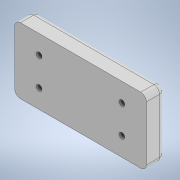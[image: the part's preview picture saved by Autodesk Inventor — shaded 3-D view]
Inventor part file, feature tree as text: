
AUTODESK INVENTOR PART (.ipt)
format: ipt  version: 2021 (Build 250183000, 183)  size: 144,896 bytes
history: native  units: mm
features: thread x4, fillet x2, sketch x2, other x1, extrude x1, hole x1
ambient origin geometry x8: Origin, YZ Plane, XZ Plane, XY Plane, X Axis, Y Axis, Z Axis, Center Point
bodies: Body1 (feature_tree)
feature tree (11):
  other  "Sólido1"
  extrude  "Extrusão1"  Depth=35.0mm
  fillet  "Arredondamento1"  Radius=10.0mm
  fillet  "Arredondamento2"  Radius=3.0mm
  hole  "Furo1"  [1 undecoded]
  thread  "Rosca1"  [1 undecoded]
  thread  "Rosca2"  [1 undecoded]
  thread  "Rosca3"  [1 undecoded]
  thread  "Rosca4"  [1 undecoded]
  sketch  "Esboço1"  dims[d0=70.0mm d1=35.0mm d2=10.0mm d3=0.0mm d4=3.0mm]
  sketch  "Esboço3"  dims[d5=3.0mm d18=10.0mm d19=10.0mm d20=10.0mm d21=10.0mm d22=10.0mm d23=10.0mm d24=10.0mm d25=10.0mm d26=3.0mm d27=6.0mm d28=5.0mm d29=2.0mm d30=90.0deg d31=3.0mm d32=20.594885mm d33=3.0mm d34=7.0mm d35=3.0mm d36=0.0mm d37=3.0mm d38=0.0mm d39=3.0mm d40=0.0mm]
note: 5 required parameter values undecoded (feature->parameter linkage not recoverable at this tier; creation-order binding heuristic only, values carry confidence <= 0.55)
